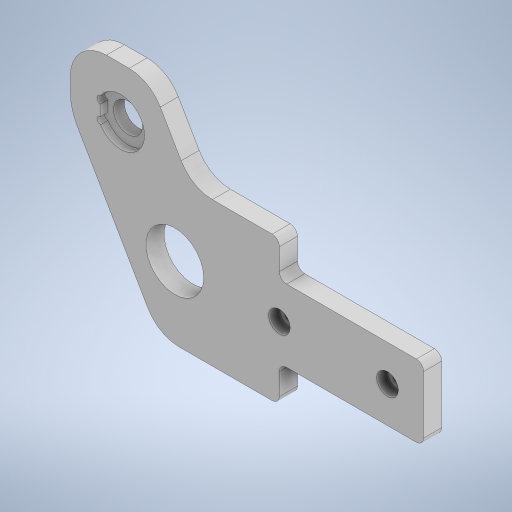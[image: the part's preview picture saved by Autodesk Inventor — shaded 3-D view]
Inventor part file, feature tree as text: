
AUTODESK INVENTOR PART (.ipt)
format: ipt  version: 2024.3 (Build 283343000, 343)  size: 348,160 bytes
history: native  units: mm
features: sketch x5, extrude x4, fillet x2, other x1, hole x1, mirror x1
ambient origin geometry x8: Origin, YZ Plane, XZ Plane, XY Plane, X Axis, Y Axis, Z Axis, Center Point
bodies: Body1 (feature_tree)
feature tree (14):
  other  "ソリッド1"
  extrude  "押し出し1"  Depth=98.0mm
  hole  "穴1"  [1 undecoded]
  fillet  "フィレット1"  Radius=40.0mm
  fillet  "フィレット2"  Radius=20.0mm
  extrude  "押し出し3"  Depth=10.0mm
  extrude  "押し出し4"  Depth=69.0mm
  mirror  "ミラー1"
  extrude  "押し出し5"  TaperAngle=30.0deg  [1 undecoded]
  sketch  "スケッチ1"
  sketch  "スケッチ2"
  sketch  "スケッチ5"
  sketch  "スケッチ6"
  sketch  "スケッチ7"
note: 2 required parameter values undecoded (feature->parameter linkage not recoverable at this tier; creation-order binding heuristic only, values carry confidence <= 0.55)
